# Revit family: BVN_BACF
name_source: partatom
category: Mechanical Equipment
units: mm (PartAtom-declared; Revit-internal decimal feet)

## family parameters
Cut with Voids When Loaded = No
Host = Face
Part Type = Normal
Room Calculation Point = No
Round Connector Dimension = Use Diameter
Shared = No

## types (20) — shared parameters
C = 40 mm  [stored 0.131234 ft]
Default Elevation = 1219 mm
Description = Roof Fan
Frequency = 50 Hz
Manufacturer = Bahçıvan Elektrik Motor San. ve Tic. Ltd. Şti.
Material = <By Category>
Model = BACF
Q_Alt = 120 mm  [stored 0.393701 ft]
URL = http://www.bahcivanmotor.com.tr

## per-type parameters (varying)
| type | A | Air Flow | B | B' | Current | F | Insulation Class | Kondansatör (uF) | Power | Protection Class | Q_Silindir | Sound Pressure Level dB(A) | Speed(d/d) | Tepe Genislik | Voltage | Weight | h_Koni | h_Silindir | h_Tepe |
| BACF 300M | 340 mm  [stored 1.11549 ft] | 2100.0 m³/h | 685 mm | 585 mm  [stored 1.91929 ft] | 1 A | 560 mm  [stored 1.83727 ft] | B | 3 | 110 W | 44 | 500 mm  [stored 1.64042 ft] | 47 | 1700 | 283 mm | 230 V | 16.00 kg | 100 mm  [stored 0.328084 ft] | 165 mm | 75 mm  [stored 0.246063 ft] |
| BACF 350M | 340 mm  [stored 1.11549 ft] | 2880.0 m³/h | 685 mm | 585 mm  [stored 1.91929 ft] | 1 A | 560 mm  [stored 1.83727 ft] | B | 6 | 310 W | 44 | 500 mm  [stored 1.64042 ft] | 48 | 1550 | 283 mm | 230 V | 18.00 kg | 100 mm  [stored 0.328084 ft] | 165 mm | 75 mm  [stored 0.246063 ft] |
| BACF 400M | 470 mm  [stored 1.54199 ft] | 4500.0 m³/h | 824 mm | 700 mm  [stored 2.29659 ft] | 1 A | 630 mm  [stored 2.06693 ft] | B | 6 | 310 W | 44 | 500 mm  [stored 1.64042 ft] | 51 | 1500 | 340 mm  [stored 1.11549 ft] | 230 V | 20.00 kg | 110 mm  [stored 0.360892 ft] | 280 mm  [stored 0.918635 ft] | 80 mm  [stored 0.262467 ft] |
| BACF 450M | 480 mm  [stored 1.5748 ft] | 7460.0 m³/h | 824 mm | 635 mm | 2 A | 710 mm | B | 8 | 390 W | 44 | 560 mm  [stored 1.83727 ft] | 55 | 1550 | 308 mm | 230 V | 25.00 kg | 110 mm  [stored 0.360892 ft] | 280 mm  [stored 0.918635 ft] | 90 mm  [stored 0.295276 ft] |
| BACF 500M | 480 mm  [stored 1.5748 ft] | 8500.0 m³/h | 824 mm | 635 mm | 2 A | 740 mm  [stored 2.42782 ft] | B | 12 | 480 W | 44 | 560 mm  [stored 1.83727 ft] | 57 | 1350 | 308 mm | 230 V | 30.00 kg | 110 mm  [stored 0.360892 ft] | 280 mm  [stored 0.918635 ft] | 90 mm  [stored 0.295276 ft] |
| BACF 560M | 450 mm  [stored 1.47638 ft] | 10400.0 m³/h | 831 mm | 625 mm  [stored 2.05052 ft] | 5 A | 800 mm | F | 0 | 750 W | 55 | 550 mm | 61 | 1405 | 303 mm | 230 V | 37.00 kg | 80 mm  [stored 0.262467 ft] | 300 mm | 70 mm  [stored 0.229659 ft] |
| BACF 630M | 540 mm  [stored 1.77165 ft] | 14000.0 m³/h | 1190 mm | 1155 mm | 7 A | 850 mm | F | 0 | 1100 W | 55 | 750 mm | 63 | 1410 | 568 mm | 230 V | 45.00 kg | 10 mm  [stored 0.0328084 ft] | 310 mm  [stored 1.01706 ft] | 220 mm  [stored 0.721785 ft] |
| BACF 710M | 540 mm  [stored 1.77165 ft] | 18000.0 m³/h | 1190 mm | 1155 mm | 9 A | 850 mm | F | 0 | 1500 W | 55 | 750 mm | 68 | 1410 | 568 mm | 230 V | 53.00 kg | 10 mm  [stored 0.0328084 ft] | 310 mm  [stored 1.01706 ft] | 220 mm  [stored 0.721785 ft] |
| BACF 900T | 600 mm  [stored 1.9685 ft] | 32000.0 m³/h | 1460 mm | 1420 mm | 7 A | 1000 mm | F | 0 | 3000 W | 55 | 940 mm | 74 | 1425 | 700 mm  [stored 2.29659 ft] | 380 V | 80.00 kg | 10 mm  [stored 0.0328084 ft] | 360 mm  [stored 1.1811 ft] | 230 mm  [stored 0.754593 ft] |
| BACF 800M | 560 mm  [stored 1.83727 ft] | 26000.0 m³/h | 1460 mm | 1420 mm | 13 A | 1000 mm | F | 0 | 2200 W | 55 | 940 mm | 70 | 1425 | 700 mm  [stored 2.29659 ft] | 230 V | 75.00 kg | 10 mm  [stored 0.0328084 ft] | 320 mm  [stored 1.04987 ft] | 230 mm  [stored 0.754593 ft] |
| BACF 1000T | 610 mm | 42000.0 m³/h | 1460 mm | 1420 mm | 8 A | 1000 mm | F | 0 | 5500 W | 55 | 940 mm | 77 | 1440 | 700 mm  [stored 2.29659 ft] | 380 V | 105.00 kg | 10 mm  [stored 0.0328084 ft] | 370 mm  [stored 1.21391 ft] | 230 mm  [stored 0.754593 ft] |
| BACF 300T | 340 mm  [stored 1.11549 ft] | 1800.0 m³/h | 685 mm | 585 mm  [stored 1.91929 ft] | 1 A | 560 mm  [stored 1.83727 ft] | B | 0 | 210 W | 44 | 500 mm  [stored 1.64042 ft] | 47 | 1445 | 283 mm | 380 V | 16.00 kg | 100 mm  [stored 0.328084 ft] | 165 mm | 75 mm  [stored 0.246063 ft] |
| BACF 350T | 340 mm  [stored 1.11549 ft] | 2600.0 m³/h | 685 mm | 585 mm  [stored 1.91929 ft] | 1 A | 560 mm  [stored 1.83727 ft] | B | 0 | 270 W | 44 | 500 mm  [stored 1.64042 ft] | 48 | 1400 | 283 mm | 380 V | 18.00 kg | 100 mm  [stored 0.328084 ft] | 165 mm | 75 mm  [stored 0.246063 ft] |
| BACF 400T | 470 mm  [stored 1.54199 ft] | 4500.0 m³/h | 824 mm | 700 mm  [stored 2.29659 ft] | 1 A | 630 mm  [stored 2.06693 ft] | B | 0 | 320 W | 44 | 500 mm  [stored 1.64042 ft] | 51 | 1600 | 340 mm  [stored 1.11549 ft] | 380 V | 20.00 kg | 110 mm  [stored 0.360892 ft] | 280 mm  [stored 0.918635 ft] | 80 mm  [stored 0.262467 ft] |
| BACF 450T | 480 mm  [stored 1.5748 ft] | 6500.0 m³/h | 824 mm | 635 mm | 2 A | 710 mm | B | 0 | 360 W | 44 | 560 mm  [stored 1.83727 ft] | 55 | 1240 | 308 mm | 380 V | 25.00 kg | 110 mm  [stored 0.360892 ft] | 280 mm  [stored 0.918635 ft] | 90 mm  [stored 0.295276 ft] |
| BACF 500T | 480 mm  [stored 1.5748 ft] | 8500.0 m³/h | 824 mm | 635 mm | 1 A | 740 mm  [stored 2.42782 ft] | B | 0 | 450 W | 44 | 560 mm  [stored 1.83727 ft] | 57 | 1260 | 308 mm | 380 V | 30.00 kg | 110 mm  [stored 0.360892 ft] | 280 mm  [stored 0.918635 ft] | 90 mm  [stored 0.295276 ft] |
| BACF 560T | 450 mm  [stored 1.47638 ft] | 10400.0 m³/h | 831 mm | 625 mm  [stored 2.05052 ft] | 2 A | 800 mm | F | 0 | 750 W | 55 | 550 mm | 61 | 1405 | 303 mm | 380 V | 37.00 kg | 80 mm  [stored 0.262467 ft] | 300 mm | 70 mm  [stored 0.229659 ft] |
| BACF 630T | 540 mm  [stored 1.77165 ft] | 14000.0 m³/h | 1190 mm | 1155 mm | 3 A | 850 mm | F | 0 | 1100 W | 55 | 750 mm | 63 | 1410 | 568 mm | 380 V | 45.00 kg | 10 mm  [stored 0.0328084 ft] | 310 mm  [stored 1.01706 ft] | 220 mm  [stored 0.721785 ft] |
| BACF 710T | 540 mm  [stored 1.77165 ft] | 18000.0 m³/h | 1190 mm | 1155 mm | 4 A | 850 mm | F | 0 | 1500 W | 55 | 750 mm | 68 | 1410 | 568 mm | 380 V | 53.00 kg | 10 mm  [stored 0.0328084 ft] | 310 mm  [stored 1.01706 ft] | 220 mm  [stored 0.721785 ft] |
| BACF 800T | 560 mm  [stored 1.83727 ft] | 26000.0 m³/h | 1460 mm | 1420 mm | 5 A | 1000 mm | F | 0 | 2200 W | 55 | 940 mm | 70 | 1425 | 700 mm  [stored 2.29659 ft] | 380 V | 75.00 kg | 10 mm  [stored 0.0328084 ft] | 320 mm  [stored 1.04987 ft] | 230 mm  [stored 0.754593 ft] |

note: [stored X ft] marks values corroborated as IEEE doubles in the binary element streams (Revit-internal decimal feet)

## geometry (parser evidence)
native form markers: Sweep x2
no freeform markers — native parametric forms only
